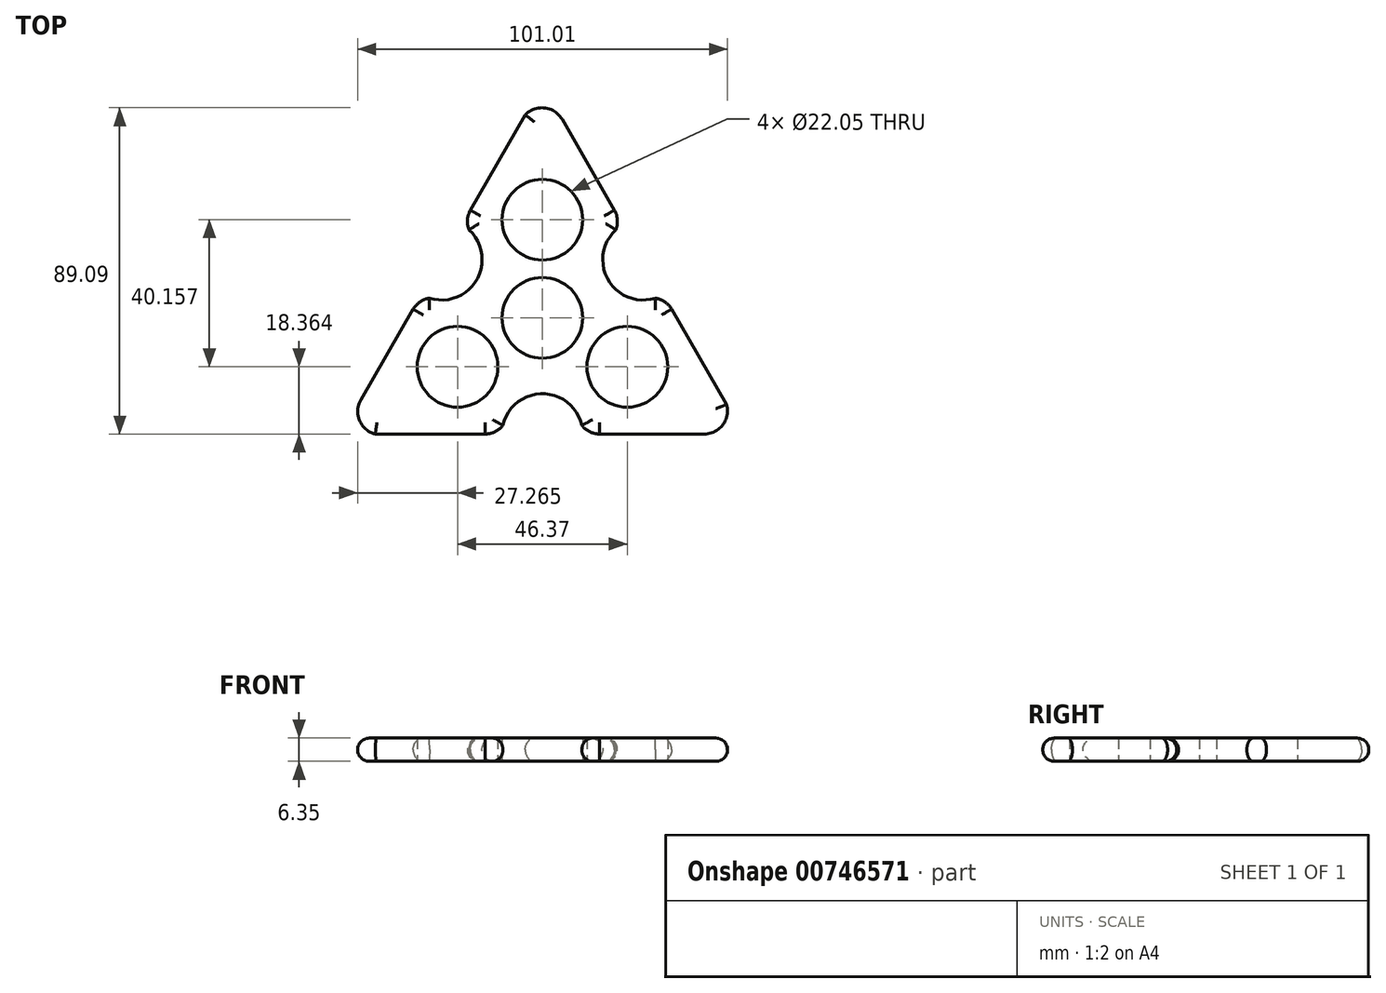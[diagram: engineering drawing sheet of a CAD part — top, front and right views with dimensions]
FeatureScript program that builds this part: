
annotation { "Feature Type Name" : "Feature", "Feature Type Description" : "" }
export const myFeature = defineFeature(function(context is Context, id is Id, definition is map)
    precondition{}
    {
        {
            var Q0;
            Q0=qCreatedBy(makeId("Top.planeOp"),FACE);
            var sketch = newSketch(context, id + "F0", { "sketchPlane" : qUnion([Q0])});
            skCircle(sketch, "E0", {"center": v(0, 0) * mm, "radius": 11.02 * mm});
            skCircle(sketch, "E1", {"center": v(0, 26.77) * mm, "radius": 11.02 * mm});
            skCircle(sketch, "E2.1.0", {"center": v(-23.18, -13.39) * mm, "radius": 11.02 * mm});
            skCircle(sketch, "E2.2.0", {"center": v(23.18, -13.39) * mm, "radius": 11.02 * mm});
            skCircle(sketch, "E3.cCircle", {"center": v(0, 0) * mm, "radius": 31.75 * mm, "construction": true});
            skLineSegment(sketch, "E3.0", {"start": v(-55, -31.75) * mm, "end": v(55, -31.75) * mm});
            skLineSegment(sketch, "E3.1", {"start": v(0, 63.5) * mm, "end": v(-55, -31.75) * mm});
            skLineSegment(sketch, "E3.2", {"start": v(55, -31.75) * mm, "end": v(0, 63.5) * mm});
            skPoint(sketch, "E3.0.midPoint", {"position": v(0, -31.75) * mm});
            skArc(sketch, "E4", {"start": v(-49.6, -22.4) * mm, "mid": v(-49.18, -29.4) * mm, "end": v(-42.58, -31.75) * mm});
            skArc(sketch, "E5.1.0", {"start": v(44.2, -31.75) * mm, "mid": v(50.05, -27.9) * mm, "end": v(48.79, -21) * mm});
            skArc(sketch, "E5.2.0", {"start": v(5.4, 54.16) * mm, "mid": v(-0.87, 57.29) * mm, "end": v(-6.2, 52.75) * mm});
            skCircle(sketch, "E6", {"center": v(0, -31.75) * mm, "radius": 11.02 * mm});
            skCircle(sketch, "E7.1.0", {"center": v(27.5, 15.87) * mm, "radius": 11.02 * mm});
            skCircle(sketch, "E7.2.0", {"center": v(-27.5, 15.88) * mm, "radius": 11.02 * mm});
            skArc(sketch, "E8", {"start": v(9.4, -26) * mm, "mid": v(11.4, -30.05) * mm, "end": v(15.6, -31.75) * mm});
            skArc(sketch, "E9.MirrorCS", {"start": v(-9.4, -26) * mm, "mid": v(-11.4, -30.05) * mm, "end": v(-15.6, -31.75) * mm});
            skArc(sketch, "E10.1.0", {"start": v(27.23, 4.85) * mm, "mid": v(31.73, 5.15) * mm, "end": v(35.3, 2.37) * mm});
            skArc(sketch, "E10.1.1", {"start": v(17.82, 21.15) * mm, "mid": v(20.32, 24.9) * mm, "end": v(19.7, 29.38) * mm});
            skArc(sketch, "E10.2.0", {"start": v(-17.82, 21.15) * mm, "mid": v(-20.32, 24.9) * mm, "end": v(-19.7, 29.38) * mm});
            skArc(sketch, "E10.2.1", {"start": v(-27.23, 4.85) * mm, "mid": v(-31.73, 5.15) * mm, "end": v(-35.3, 2.37) * mm});
            skSolve(sketch);
        }
        {
            var Q0;
            Q0=makeQuery(id+"F0.imprint","IMPRINT",FACE,{"disambiguationData":[TD([[makeQuery(id+"F0.imprint","IMPRINT",EDGE,{"derivedFrom":sQuery(id+"F0.wireOp",EDGE,"E0")}),-1.0]])]});
            extrude(context, id + "F1", {"entities" : qUnion([Q0]), "depth" : 6.35 * mm, "offsetDistance" : 25.4 * mm});
        }
        {
            var Q0;
            {var subQ0=sQuery(id+"F0.wireOp",EDGE,"E5.2.0");var subQ1=sQuery(id+"F0.wireOp",EDGE,"E3.1");var subQ2=makeQuery(id+"F0.imprint","INTERSECT",VERTEX,{"disambiguationData":[OD(0.0)],"derivedFrom":[subQ1,subQ0]});Q0=makeQuery(id+"F1.opExtrude","CAP_EDGE",EDGE,{"disambiguationData":[OSD([subQ1]),TDD([makeQuery(id+"F0.imprint","IMPRINT",EDGE,{"disambiguationData":[TD([[subQ2,1.0]])],"derivedFrom":subQ1}),makeQuery(id+"F0.imprint","IMPRINT",EDGE,{"disambiguationData":[TD([[subQ2,-1.0]])],"derivedFrom":subQ1})])],"isStart":false});}
            var Q1;
            Q1=makeQuery(id+"F1.opExtrude","CAP_EDGE",EDGE,{"disambiguationData":[OSD([sQuery(id+"F0.wireOp",EDGE,"E5.2.0")])],"isStart":false});
            var Q2;
            {var subQ0=sQuery(id+"F0.wireOp",EDGE,"E3.2");Q2=makeQuery(id+"F1.opExtrude","CAP_EDGE",EDGE,{"disambiguationData":[OSD([subQ0]),TDD([makeQuery(id+"F0.imprint","IMPRINT",EDGE,{"disambiguationData":[TD([[makeQuery(id+"F0.imprint","INTERSECT",VERTEX,{"disambiguationData":[OD(0.0)],"derivedFrom":[subQ0,sQuery(id+"F0.wireOp",EDGE,"E5.2.0")]}),1.0]])],"derivedFrom":subQ0})])],"isStart":false});}
            var Q3;
            Q3=makeQuery(id+"F1.opExtrude","CAP_EDGE",EDGE,{"disambiguationData":[OSD([sQuery(id+"F0.wireOp",EDGE,"E7.1.0")])],"isStart":false});
            var Q4;
            {var subQ0=sQuery(id+"F0.wireOp",EDGE,"E5.1.0");var subQ1=sQuery(id+"F0.wireOp",EDGE,"E3.2");var subQ2=makeQuery(id+"F0.imprint","INTERSECT",VERTEX,{"disambiguationData":[OD(0.0)],"derivedFrom":[subQ1,subQ0]});Q4=makeQuery(id+"F1.opExtrude","CAP_EDGE",EDGE,{"disambiguationData":[OSD([subQ1]),TDD([makeQuery(id+"F0.imprint","IMPRINT",EDGE,{"disambiguationData":[TD([[subQ2,1.0]])],"derivedFrom":subQ1}),makeQuery(id+"F0.imprint","IMPRINT",EDGE,{"disambiguationData":[TD([[subQ2,-1.0]])],"derivedFrom":subQ1})])],"isStart":false});}
            var Q5;
            Q5=makeQuery(id+"F1.opExtrude","CAP_EDGE",EDGE,{"disambiguationData":[OSD([sQuery(id+"F0.wireOp",EDGE,"E5.1.0")])],"isStart":false});
            var Q6;
            Q6=makeQuery(id+"F1.opExtrude","CAP_EDGE",EDGE,{"disambiguationData":[OSD([sQuery(id+"F0.wireOp",EDGE,"E6")])],"isStart":false});
            var Q7;
            {var subQ0=sQuery(id+"F0.wireOp",EDGE,"E3.0");Q7=makeQuery(id+"F1.opExtrude","CAP_EDGE",EDGE,{"disambiguationData":[OSD([subQ0]),TDD([makeQuery(id+"F0.imprint","IMPRINT",EDGE,{"disambiguationData":[TD([[makeQuery(id+"F0.imprint","INTERSECT",VERTEX,{"disambiguationData":[OD(0.0)],"derivedFrom":[subQ0,sQuery(id+"F0.wireOp",EDGE,"E5.1.0")]}),1.0]])],"derivedFrom":subQ0})])],"isStart":false});}
            var Q8;
            Q8=makeQuery(id+"F1.opExtrude","CAP_EDGE",EDGE,{"disambiguationData":[OSD([sQuery(id+"F0.wireOp",EDGE,"E4")])],"isStart":false});
            var Q9;
            {var subQ0=sQuery(id+"F0.wireOp",EDGE,"E4");var subQ1=sQuery(id+"F0.wireOp",EDGE,"E3.0");var subQ2=makeQuery(id+"F0.imprint","INTERSECT",VERTEX,{"disambiguationData":[OD(0.0)],"derivedFrom":[subQ1,subQ0]});Q9=makeQuery(id+"F1.opExtrude","CAP_EDGE",EDGE,{"disambiguationData":[OSD([subQ1]),TDD([makeQuery(id+"F0.imprint","IMPRINT",EDGE,{"disambiguationData":[TD([[subQ2,1.0]])],"derivedFrom":subQ1}),makeQuery(id+"F0.imprint","IMPRINT",EDGE,{"disambiguationData":[TD([[subQ2,-1.0]])],"derivedFrom":subQ1})])],"isStart":false});}
            var Q10;
            {var subQ0=sQuery(id+"F0.wireOp",EDGE,"E3.1");Q10=makeQuery(id+"F1.opExtrude","CAP_EDGE",EDGE,{"disambiguationData":[OSD([subQ0]),TDD([makeQuery(id+"F0.imprint","IMPRINT",EDGE,{"disambiguationData":[TD([[makeQuery(id+"F0.imprint","INTERSECT",VERTEX,{"disambiguationData":[OD(0.0)],"derivedFrom":[subQ0,sQuery(id+"F0.wireOp",EDGE,"E4")]}),1.0]])],"derivedFrom":subQ0})])],"isStart":false});}
            var Q11;
            Q11=makeQuery(id+"F1.opExtrude","CAP_EDGE",EDGE,{"disambiguationData":[OSD([sQuery(id+"F0.wireOp",EDGE,"E7.2.0")])],"isStart":false});
            fillet(context, id + "F2", {"entities" : qUnion([Q0, Q1, Q2, Q3, Q4, Q5, Q6, Q7, Q8, Q9, Q10, Q11]), "radius" : 3.17 * mm, "tangentPropagation" : true, "allowEdgeOverflow" : false});
        }
        {
            var Q0;
            {var subQ0=sQuery(id+"F0.wireOp",EDGE,"E4");var subQ1=sQuery(id+"F0.wireOp",EDGE,"E3.0");var subQ2=makeQuery(id+"F0.imprint","INTERSECT",VERTEX,{"disambiguationData":[OD(0.0)],"derivedFrom":[subQ1,subQ0]});Q0=makeQuery(id+"F1.opExtrude","CAP_EDGE",EDGE,{"disambiguationData":[OSD([subQ1]),TDD([makeQuery(id+"F0.imprint","IMPRINT",EDGE,{"disambiguationData":[TD([[subQ2,1.0]])],"derivedFrom":subQ1}),makeQuery(id+"F0.imprint","IMPRINT",EDGE,{"disambiguationData":[TD([[subQ2,-1.0]])],"derivedFrom":subQ1})])],"isStart":true});}
            var Q1;
            Q1=makeQuery(id+"F1.opExtrude","CAP_EDGE",EDGE,{"disambiguationData":[OSD([sQuery(id+"F0.wireOp",EDGE,"E4")])],"isStart":true});
            var Q2;
            Q2=makeQuery(id+"F1.opExtrude","CAP_EDGE",EDGE,{"disambiguationData":[OSD([sQuery(id+"F0.wireOp",EDGE,"E5.1.0")])],"isStart":true});
            var Q3;
            Q3=makeQuery(id+"F1.opExtrude","CAP_EDGE",EDGE,{"disambiguationData":[OSD([sQuery(id+"F0.wireOp",EDGE,"E5.2.0")])],"isStart":true});
            var Q4;
            {var subQ0=sQuery(id+"F0.wireOp",EDGE,"E5.2.0");var subQ1=sQuery(id+"F0.wireOp",EDGE,"E3.1");var subQ2=makeQuery(id+"F0.imprint","INTERSECT",VERTEX,{"disambiguationData":[OD(0.0)],"derivedFrom":[subQ1,subQ0]});Q4=makeQuery(id+"F1.opExtrude","CAP_EDGE",EDGE,{"disambiguationData":[OSD([subQ1]),TDD([makeQuery(id+"F0.imprint","IMPRINT",EDGE,{"disambiguationData":[TD([[subQ2,1.0]])],"derivedFrom":subQ1}),makeQuery(id+"F0.imprint","IMPRINT",EDGE,{"disambiguationData":[TD([[subQ2,-1.0]])],"derivedFrom":subQ1})])],"isStart":true});}
            var Q5;
            {var subQ0=sQuery(id+"F0.wireOp",EDGE,"E3.2");Q5=makeQuery(id+"F1.opExtrude","CAP_EDGE",EDGE,{"disambiguationData":[OSD([subQ0]),TDD([makeQuery(id+"F0.imprint","IMPRINT",EDGE,{"disambiguationData":[TD([[makeQuery(id+"F0.imprint","INTERSECT",VERTEX,{"disambiguationData":[OD(0.0)],"derivedFrom":[subQ0,sQuery(id+"F0.wireOp",EDGE,"E5.2.0")]}),1.0]])],"derivedFrom":subQ0})])],"isStart":true});}
            var Q6;
            Q6=makeQuery(id+"F1.opExtrude","CAP_EDGE",EDGE,{"disambiguationData":[OSD([sQuery(id+"F0.wireOp",EDGE,"E7.1.0")])],"isStart":true});
            var Q7;
            Q7=makeQuery(id+"F1.opExtrude","CAP_EDGE",EDGE,{"disambiguationData":[OSD([sQuery(id+"F0.wireOp",EDGE,"E7.2.0")])],"isStart":true});
            var Q8;
            Q8=makeQuery(id+"F1.opExtrude","CAP_EDGE",EDGE,{"disambiguationData":[OSD([sQuery(id+"F0.wireOp",EDGE,"E6")])],"isStart":true});
            var Q9;
            {var subQ0=sQuery(id+"F0.wireOp",EDGE,"E3.1");Q9=makeQuery(id+"F1.opExtrude","CAP_EDGE",EDGE,{"disambiguationData":[OSD([subQ0]),TDD([makeQuery(id+"F0.imprint","IMPRINT",EDGE,{"disambiguationData":[TD([[makeQuery(id+"F0.imprint","INTERSECT",VERTEX,{"disambiguationData":[OD(0.0)],"derivedFrom":[subQ0,sQuery(id+"F0.wireOp",EDGE,"E4")]}),1.0]])],"derivedFrom":subQ0})])],"isStart":true});}
            var Q10;
            {var subQ0=sQuery(id+"F0.wireOp",EDGE,"E5.1.0");var subQ1=sQuery(id+"F0.wireOp",EDGE,"E3.2");var subQ2=makeQuery(id+"F0.imprint","INTERSECT",VERTEX,{"disambiguationData":[OD(0.0)],"derivedFrom":[subQ1,subQ0]});Q10=makeQuery(id+"F1.opExtrude","CAP_EDGE",EDGE,{"disambiguationData":[OSD([subQ1]),TDD([makeQuery(id+"F0.imprint","IMPRINT",EDGE,{"disambiguationData":[TD([[subQ2,1.0]])],"derivedFrom":subQ1}),makeQuery(id+"F0.imprint","IMPRINT",EDGE,{"disambiguationData":[TD([[subQ2,-1.0]])],"derivedFrom":subQ1})])],"isStart":true});}
            var Q11;
            {var subQ0=sQuery(id+"F0.wireOp",EDGE,"E3.0");Q11=makeQuery(id+"F1.opExtrude","CAP_EDGE",EDGE,{"disambiguationData":[OSD([subQ0]),TDD([makeQuery(id+"F0.imprint","IMPRINT",EDGE,{"disambiguationData":[TD([[makeQuery(id+"F0.imprint","INTERSECT",VERTEX,{"disambiguationData":[OD(0.0)],"derivedFrom":[subQ0,sQuery(id+"F0.wireOp",EDGE,"E5.1.0")]}),1.0]])],"derivedFrom":subQ0})])],"isStart":true});}
            fillet(context, id + "F3", {"entities" : qUnion([Q0, Q1, Q2, Q3, Q4, Q5, Q6, Q7, Q8, Q9, Q10, Q11]), "radius" : 3.17 * mm, "tangentPropagation" : true, "allowEdgeOverflow" : false});
        }
    });
